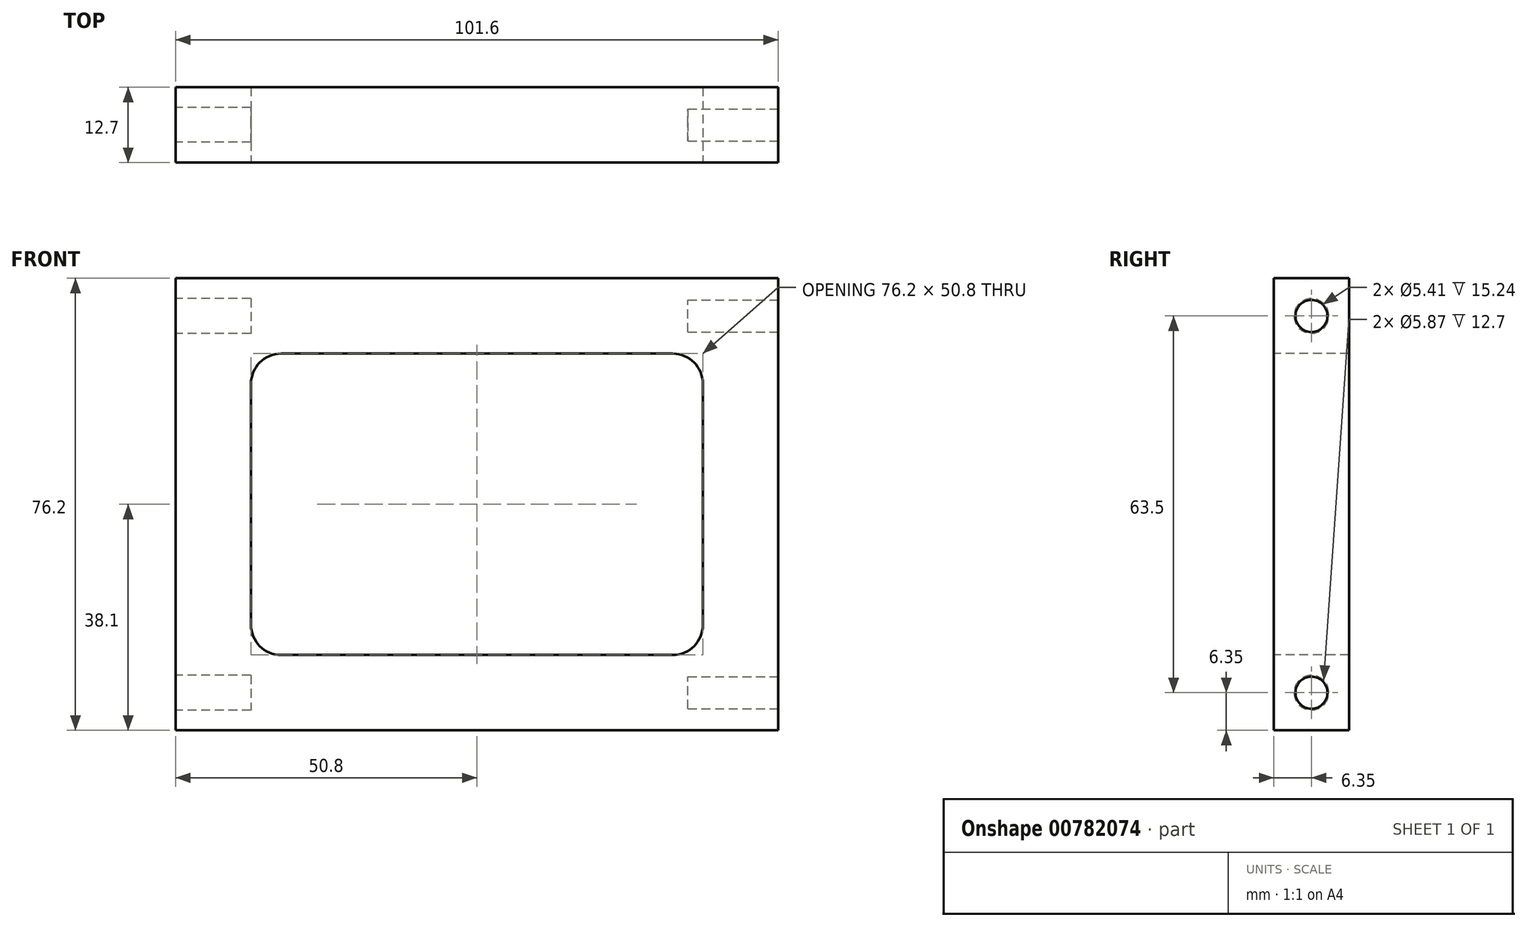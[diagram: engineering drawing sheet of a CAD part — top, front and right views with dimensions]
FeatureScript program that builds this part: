
annotation { "Feature Type Name" : "Feature", "Feature Type Description" : "" }
export const myFeature = defineFeature(function(context is Context, id is Id, definition is map)
    precondition{}
    {
        {
            var Q0;
            Q0=qCreatedBy(makeId("Front.planeOp"),FACE);
            var sketch = newSketch(context, id + "F0", { "sketchPlane" : qUnion([Q0])});
            skLineSegment(sketch, "E0.bottom", {"start": v(0, 0) * mm, "end": v(101.6, 0) * mm});
            skLineSegment(sketch, "E0.top", {"start": v(0, 76.2) * mm, "end": v(101.6, 76.2) * mm});
            skLineSegment(sketch, "E0.left", {"start": v(0, 0) * mm, "end": v(0, 76.2) * mm});
            skLineSegment(sketch, "E0.right", {"start": v(101.6, 0) * mm, "end": v(101.6, 76.2) * mm});
            skSolve(sketch);
        }
        {
            var Q0;
            Q0 = qSketchRegion(id + "F0", true);
            extrude(context, id + "F1", {"entities" : qUnion([Q0]), "depth" : 12.7 * mm, "offsetDistance" : 25.4 * mm});
        }
        {
            var Q0;
            Q0=makeQuery(id+"F1.opExtrude","SWEPT_FACE",FACE,{"disambiguationData":[OSD([sQuery(id+"F0.wireOp",EDGE,"E0.right")])]});
            var sketch = newSketch(context, id + "F2", { "sketchPlane" : qUnion([Q0])});
            skCircle(sketch, "E1", {"center": v(-6.35, 69.85) * mm, "radius": 2.7 * mm});
            skCircle(sketch, "E2", {"center": v(-6.35, 6.35) * mm, "radius": 2.7 * mm});
            skSolve(sketch);
        }
        {
            var Q0;
            Q0 = qSketchRegion(id + "F2", true);
            extrude(context, id + "F3", {"entities" : qUnion([Q0]), "operationType" : NewBodyOperationType.REMOVE, "oppositeDirection" : true, "depth" : 15.24 * mm, "offsetDistance" : 25.4 * mm});
        }
        {
            var Q0;
            Q0=makeQuery(id+"F1.opExtrude","SWEPT_FACE",FACE,{"disambiguationData":[OSD([sQuery(id+"F0.wireOp",EDGE,"E0.left")])]});
            var sketch = newSketch(context, id + "F4", { "sketchPlane" : qUnion([Q0])});
            skCircle(sketch, "E3", {"center": v(6.35, 69.85) * mm, "radius": 2.93 * mm});
            skCircle(sketch, "E4", {"center": v(6.35, 6.35) * mm, "radius": 2.93 * mm});
            skSolve(sketch);
        }
        {
            var Q0;
            Q0 = qSketchRegion(id + "F4", true);
            extrude(context, id + "F5", {"entities" : qUnion([Q0]), "operationType" : NewBodyOperationType.REMOVE, "oppositeDirection" : true, "depth" : 12.7 * mm, "offsetDistance" : 25.4 * mm});
        }
        {
            var Q0;
            Q0=makeQuery(id+"F1.opExtrude","CAP_FACE",FACE,{"disambiguationData":[OSD([sQuery(id+"F0.wireOp",EDGE,"E0.bottom"),sQuery(id+"F0.wireOp",EDGE,"E0.top"),sQuery(id+"F0.wireOp",EDGE,"E0.left"),sQuery(id+"F0.wireOp",EDGE,"E0.right")])],"isStart":false});
            var sketch = newSketch(context, id + "F6", { "sketchPlane" : qUnion([Q0])});
            skLineSegment(sketch, "E5.bottom", {"start": v(12.7, 12.7) * mm, "end": v(88.9, 12.7) * mm});
            skLineSegment(sketch, "E5.top", {"start": v(12.7, 63.5) * mm, "end": v(88.9, 63.5) * mm});
            skLineSegment(sketch, "E5.left", {"start": v(12.7, 12.7) * mm, "end": v(12.7, 63.5) * mm});
            skLineSegment(sketch, "E5.right", {"start": v(88.9, 12.7) * mm, "end": v(88.9, 63.5) * mm});
            skSolve(sketch);
        }
        {
            var Q0;
            Q0 = qSketchRegion(id + "F6", true);
            extrude(context, id + "F7", {"entities" : qUnion([Q0]), "operationType" : NewBodyOperationType.REMOVE, "oppositeDirection" : true, "depth" : 25.4 * mm, "offsetDistance" : 25.4 * mm});
        }
        {
            var Q0;
            Q0=makeQuery(id+"F7.boolean.opBoolean","COPY",EDGE,{"derivedFrom":makeQuery(id+"F7.opExtrude","SWEPT_EDGE",EDGE,{"disambiguationData":[OSD([sQuery(id+"F6.wireOp",EDGE,"E5.bottom"),sQuery(id+"F6.wireOp",EDGE,"E5.left")])]})});
            var Q1;
            Q1=makeQuery(id+"F7.boolean.opBoolean","COPY",EDGE,{"derivedFrom":makeQuery(id+"F7.opExtrude","SWEPT_EDGE",EDGE,{"disambiguationData":[OSD([sQuery(id+"F6.wireOp",EDGE,"E5.top"),sQuery(id+"F6.wireOp",EDGE,"E5.right")])]})});
            var Q2;
            Q2=makeQuery(id+"F7.boolean.opBoolean","COPY",EDGE,{"derivedFrom":makeQuery(id+"F7.opExtrude","SWEPT_EDGE",EDGE,{"disambiguationData":[OSD([sQuery(id+"F6.wireOp",EDGE,"E5.bottom"),sQuery(id+"F6.wireOp",EDGE,"E5.right")])]})});
            var Q3;
            Q3=makeQuery(id+"F7.boolean.opBoolean","COPY",EDGE,{"derivedFrom":makeQuery(id+"F7.opExtrude","SWEPT_EDGE",EDGE,{"disambiguationData":[OSD([sQuery(id+"F6.wireOp",EDGE,"E5.top"),sQuery(id+"F6.wireOp",EDGE,"E5.left")])]})});
            fillet(context, id + "F8", {"entities" : qUnion([Q0, Q1, Q2, Q3]), "radius" : 5.08 * mm, "tangentPropagation" : true, "allowEdgeOverflow" : false});
        }
    });
